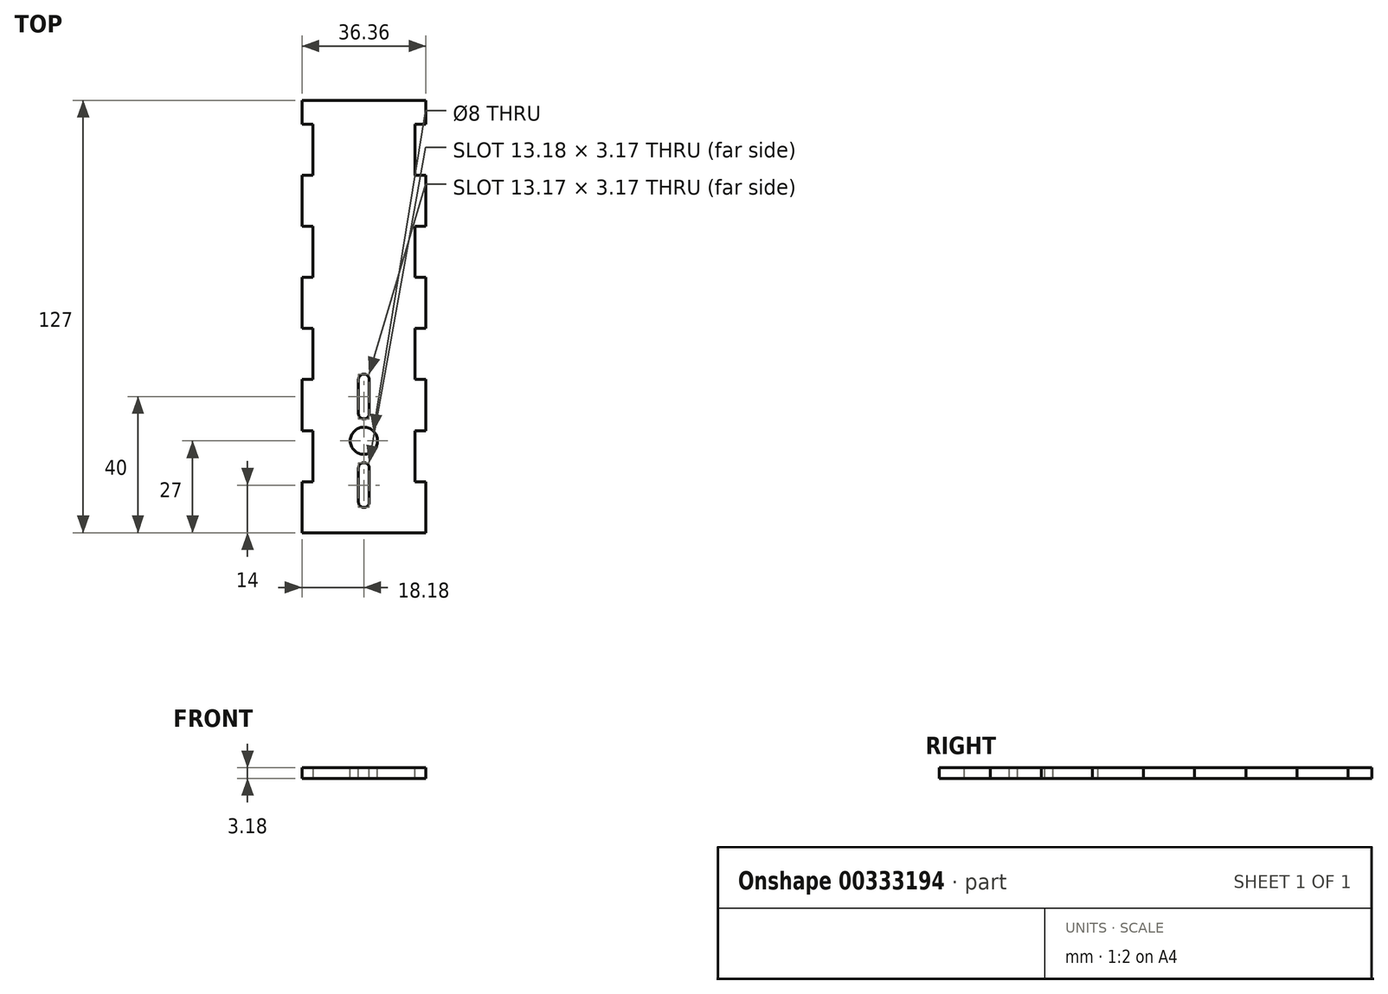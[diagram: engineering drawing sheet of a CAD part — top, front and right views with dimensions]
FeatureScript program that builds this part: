
annotation { "Feature Type Name" : "Feature", "Feature Type Description" : "" }
export const myFeature = defineFeature(function(context is Context, id is Id, definition is map)
    precondition{}
    {
        {
            var Q0;
            Q0=qCreatedBy(makeId("Top.planeOp"),FACE);
            var sketch = newSketch(context, id + "F0", { "sketchPlane" : qUnion([Q0])});
            skLineSegment(sketch, "E0.bottom", {"start": v(18.17, -41) * mm, "end": v(-18.17, -41) * mm});
            skLineSegment(sketch, "E0.top", {"start": v(18.18, 41) * mm, "end": v(-18.18, 41) * mm});
            skLineSegment(sketch, "E0.left", {"start": v(18.17, -41) * mm, "end": v(18.17, 41) * mm});
            skLineSegment(sketch, "E0.right", {"start": v(-18.17, -41) * mm, "end": v(-18.17, 41) * mm});
            skPoint(sketch, "E0.middle", {"position": v(0, 0) * mm});
            skLineSegment(sketch, "E1", {"start": v(-18.18, -26) * mm, "end": v(-15, -26) * mm});
            skLineSegment(sketch, "E2", {"start": v(-15, -26) * mm, "end": v(-15, -41) * mm});
            skLineSegment(sketch, "E3.MirrorCS", {"start": v(15, -26) * mm, "end": v(15, -41) * mm});
            skLineSegment(sketch, "E4.MirrorCS", {"start": v(18.18, -26) * mm, "end": v(15, -26) * mm});
            skLineSegment(sketch, "E5.0.1.0", {"start": v(-15, 4) * mm, "end": v(-15, -11) * mm});
            skLineSegment(sketch, "E5.0.1.1", {"start": v(-18.18, 4) * mm, "end": v(-15, 4) * mm});
            skLineSegment(sketch, "E5.0.1.2", {"start": v(18.18, 4) * mm, "end": v(15, 4) * mm});
            skLineSegment(sketch, "E5.0.1.3", {"start": v(15, 4) * mm, "end": v(15, -11) * mm});
            skLineSegment(sketch, "E5.0.2.0", {"start": v(-15, 34) * mm, "end": v(-15, 19) * mm});
            skLineSegment(sketch, "E5.0.2.1", {"start": v(-18.18, 34) * mm, "end": v(-15, 34) * mm});
            skLineSegment(sketch, "E5.0.2.2", {"start": v(18.18, 34) * mm, "end": v(15, 34) * mm});
            skLineSegment(sketch, "E5.0.2.3", {"start": v(15, 34) * mm, "end": v(15, 19) * mm});
            skLineSegment(sketch, "E5.direction1", {"start": v(-15, -41) * mm, "end": v(13.18, -41) * mm, "construction": true});
            skLineSegment(sketch, "E5.direction2", {"start": v(-15, -41) * mm, "end": v(-15, -11) * mm, "construction": true});
            skLineSegment(sketch, "E6", {"start": v(-15, -11) * mm, "end": v(-18.18, -11) * mm});
            skLineSegment(sketch, "E7", {"start": v(15, -11) * mm, "end": v(18.18, -11) * mm});
            skLineSegment(sketch, "E8", {"start": v(15, 19) * mm, "end": v(18.18, 19) * mm});
            skLineSegment(sketch, "E9", {"start": v(-15, 19) * mm, "end": v(-18.18, 19) * mm});
            skSolve(sketch);
        }
        {
            var Q0;
            {var subQ11=sQuery(id+"F0.wireOp",EDGE,"E0.top");Q0=makeQuery(id+"F0.imprint","IMPRINT",FACE,{"disambiguationData":[TD([[makeQuery(id+"F0.imprint","IMPRINT",EDGE,{"derivedFrom":subQ11}),1.0]])]});}
            extrude(context, id + "F1", {"entities" : qUnion([Q0]), "depth" : 3.17 * mm});
        }
        {
            var Q0;
            Q0=makeQuery(id+"F1.opExtrude","SWEPT_FACE",FACE,{"disambiguationData":[OSD([sQuery(id+"F0.wireOp",EDGE,"E0.bottom")])]});
            extrude(context, id + "F2", {"entities" : qUnion([Q0]), "operationType" : NewBodyOperationType.ADD, "depth" : 45 * mm});
        }
        {
            var Q0;
            Q0=makeQuery(id+"F1.opExtrude","CAP_FACE",FACE,{"disambiguationData":[OSD([sQuery(id+"F0.wireOp",EDGE,"E0.bottom"),sQuery(id+"F0.wireOp",EDGE,"E0.top"),sQuery(id+"F0.wireOp",EDGE,"E0.left"),sQuery(id+"F0.wireOp",EDGE,"E0.right"),sQuery(id+"F0.wireOp",EDGE,"E1"),sQuery(id+"F0.wireOp",EDGE,"E2"),sQuery(id+"F0.wireOp",EDGE,"E3.MirrorCS"),sQuery(id+"F0.wireOp",EDGE,"E4.MirrorCS"),sQuery(id+"F0.wireOp",EDGE,"E5.0.1.0"),sQuery(id+"F0.wireOp",EDGE,"E5.0.1.1"),sQuery(id+"F0.wireOp",EDGE,"E5.0.1.2"),sQuery(id+"F0.wireOp",EDGE,"E5.0.1.3"),sQuery(id+"F0.wireOp",EDGE,"E5.0.2.0"),sQuery(id+"F0.wireOp",EDGE,"E5.0.2.1"),sQuery(id+"F0.wireOp",EDGE,"E5.0.2.2"),sQuery(id+"F0.wireOp",EDGE,"E5.0.2.3"),sQuery(id+"F0.wireOp",EDGE,"E6"),sQuery(id+"F0.wireOp",EDGE,"E7"),sQuery(id+"F0.wireOp",EDGE,"E8"),sQuery(id+"F0.wireOp",EDGE,"E9")])],"isStart":false});
            var sketch = newSketch(context, id + "F3", { "sketchPlane" : qUnion([Q0])});
            skCircle(sketch, "E10", {"center": v(0, -59) * mm, "radius": 4 * mm});
            skLineSegment(sketch, "E11.bottom", {"start": v(1.59, -51) * mm, "end": v(-1.59, -51) * mm});
            skLineSegment(sketch, "E11.top", {"start": v(1.59, -41) * mm, "end": v(-1.59, -41) * mm});
            skLineSegment(sketch, "E11.left", {"start": v(1.59, -51) * mm, "end": v(1.59, -41) * mm});
            skLineSegment(sketch, "E11.right", {"start": v(-1.59, -51) * mm, "end": v(-1.59, -41) * mm});
            skPoint(sketch, "E11.middle", {"position": v(0, -46) * mm});
            skArc(sketch, "E12", {"start": v(1.59, -41) * mm, "mid": v(0, -39.41) * mm, "end": v(-1.59, -41) * mm});
            skArc(sketch, "E13", {"start": v(-1.59, -51) * mm, "mid": v(0, -52.59) * mm, "end": v(1.59, -51) * mm});
            skLineSegment(sketch, "E14", {"start": v(0, -59) * mm, "end": v(3.24, -59) * mm, "construction": true});
            skLineSegment(sketch, "E15.MirrorCS", {"start": v(1.59, -77) * mm, "end": v(-1.59, -77) * mm});
            skLineSegment(sketch, "E16.MirrorCS", {"start": v(1.59, -67) * mm, "end": v(-1.59, -67) * mm});
            skArc(sketch, "E17.MirrorCS", {"start": v(-1.59, -67) * mm, "mid": v(0, -65.41) * mm, "end": v(1.59, -67) * mm});
            skArc(sketch, "E18.MirrorCS", {"start": v(1.59, -77) * mm, "mid": v(0, -78.59) * mm, "end": v(-1.59, -77) * mm});
            skLineSegment(sketch, "E19.MirrorCS", {"start": v(1.59, -67) * mm, "end": v(1.59, -77) * mm});
            skLineSegment(sketch, "E20.MirrorCS", {"start": v(-1.59, -67) * mm, "end": v(-1.59, -77) * mm});
            skPoint(sketch, "E21.MirrorP", {"position": v(0, -72) * mm});
            skSolve(sketch);
        }
        {
            var Q0;
            Q0=qSketchRegion(id+"F3",true);
            extrude(context, id + "F4", {"entities" : qUnion([Q0]), "operationType" : NewBodyOperationType.REMOVE, "oppositeDirection" : true, "depth" : 25 * mm});
        }
        {
            var Q0;
            {var subQ0=sQuery(id+"F0.wireOp",EDGE,"E3.MirrorCS");Q0=makeQuery(id+"F2.boolean.opBoolean","MERGE",FACE,{"derivedFrom":[makeQuery(id+"F1.opExtrude","SWEPT_FACE",FACE,{"disambiguationData":[OSD([subQ0])]}),makeQuery(id+"F2.opExtrude","SWEPT_FACE",FACE,{"disambiguationData":[OSD([sQuery(id+"F0.wireOp",EDGE,"E0.bottom"),subQ0])]})]});}
            var sketch = newSketch(context, id + "F5", { "sketchPlane" : qUnion([Q0])});
            skLineSegment(sketch, "E22.bottom", {"start": v(-41, 0) * mm, "end": v(-56, 0) * mm});
            skLineSegment(sketch, "E22.top", {"start": v(-41, 3.17) * mm, "end": v(-56, 3.17) * mm});
            skLineSegment(sketch, "E22.left", {"start": v(-41, 0) * mm, "end": v(-41, 3.18) * mm});
            skLineSegment(sketch, "E22.right", {"start": v(-56, 0) * mm, "end": v(-56, 3.17) * mm});
            skLineSegment(sketch, "E23.1.0.0", {"start": v(-86, 0) * mm, "end": v(-86, 3.17) * mm});
            skLineSegment(sketch, "E23.1.0.1", {"start": v(-71, 0) * mm, "end": v(-71, 3.18) * mm});
            skLineSegment(sketch, "E23.direction1", {"start": v(-56, 0) * mm, "end": v(-86, 0) * mm, "construction": true});
            skSolve(sketch);
        }
        {
            var Q0;
            {var subQ0=sQuery(id+"F5.wireOp",EDGE,"E23.1.0.0");Q0=makeQuery(id+"F5.imprint","IMPRINT",FACE,{"disambiguationData":[TD([[makeQuery(id+"F5.imprint","IMPRINT",EDGE,{"derivedFrom":subQ0}),1.0]])]});}
            var Q1;
            Q1=makeQuery(id+"F5.imprint","IMPRINT",FACE,{"disambiguationData":[TD([[makeQuery(id+"F5.imprint","IMPRINT",EDGE,{"derivedFrom":sQuery(id+"F5.wireOp",EDGE,"E22.bottom")}),-1.0]])]});
            extrude(context, id + "F6", {"entities" : qUnion([Q0, Q1]), "operationType" : NewBodyOperationType.ADD, "depth" : 3.17 * mm});
        }
        {
            var Q0;
            {var subQ0=sQuery(id+"F0.wireOp",EDGE,"E2");Q0=makeQuery(id+"F2.boolean.opBoolean","MERGE",FACE,{"derivedFrom":[makeQuery(id+"F1.opExtrude","SWEPT_FACE",FACE,{"disambiguationData":[OSD([subQ0])]}),makeQuery(id+"F2.opExtrude","SWEPT_FACE",FACE,{"disambiguationData":[OSD([sQuery(id+"F0.wireOp",EDGE,"E0.bottom"),subQ0])]})]});}
            var sketch = newSketch(context, id + "F7", { "sketchPlane" : qUnion([Q0])});
            skLineSegment(sketch, "E24.bottom", {"start": v(41, 3.17) * mm, "end": v(56, 3.17) * mm});
            skLineSegment(sketch, "E24.top", {"start": v(41, 0) * mm, "end": v(56, 0) * mm});
            skLineSegment(sketch, "E24.left", {"start": v(41, 3.17) * mm, "end": v(41, 0) * mm});
            skLineSegment(sketch, "E24.right", {"start": v(56, 3.17) * mm, "end": v(56, 0) * mm});
            skLineSegment(sketch, "E25.1.0.0", {"start": v(71, 3.17) * mm, "end": v(71, 0) * mm});
            skLineSegment(sketch, "E25.1.0.1", {"start": v(86, 3.17) * mm, "end": v(86, 0) * mm});
            skLineSegment(sketch, "E25.direction1", {"start": v(41, 0) * mm, "end": v(71, 0) * mm, "construction": true});
            skSolve(sketch);
        }
        {
            var Q0;
            Q0=makeQuery(id+"F7.imprint","IMPRINT",FACE,{"disambiguationData":[TD([[makeQuery(id+"F7.imprint","IMPRINT",EDGE,{"derivedFrom":sQuery(id+"F7.wireOp",EDGE,"E24.bottom")}),-1.0]])]});
            var Q1;
            {var subQ0=sQuery(id+"F7.wireOp",EDGE,"E25.1.0.0");Q1=makeQuery(id+"F7.imprint","IMPRINT",FACE,{"disambiguationData":[TD([[makeQuery(id+"F7.imprint","IMPRINT",EDGE,{"derivedFrom":subQ0}),1.0]])]});}
            extrude(context, id + "F8", {"entities" : qUnion([Q0, Q1]), "operationType" : NewBodyOperationType.ADD, "depth" : 3.17 * mm});
        }
    });
